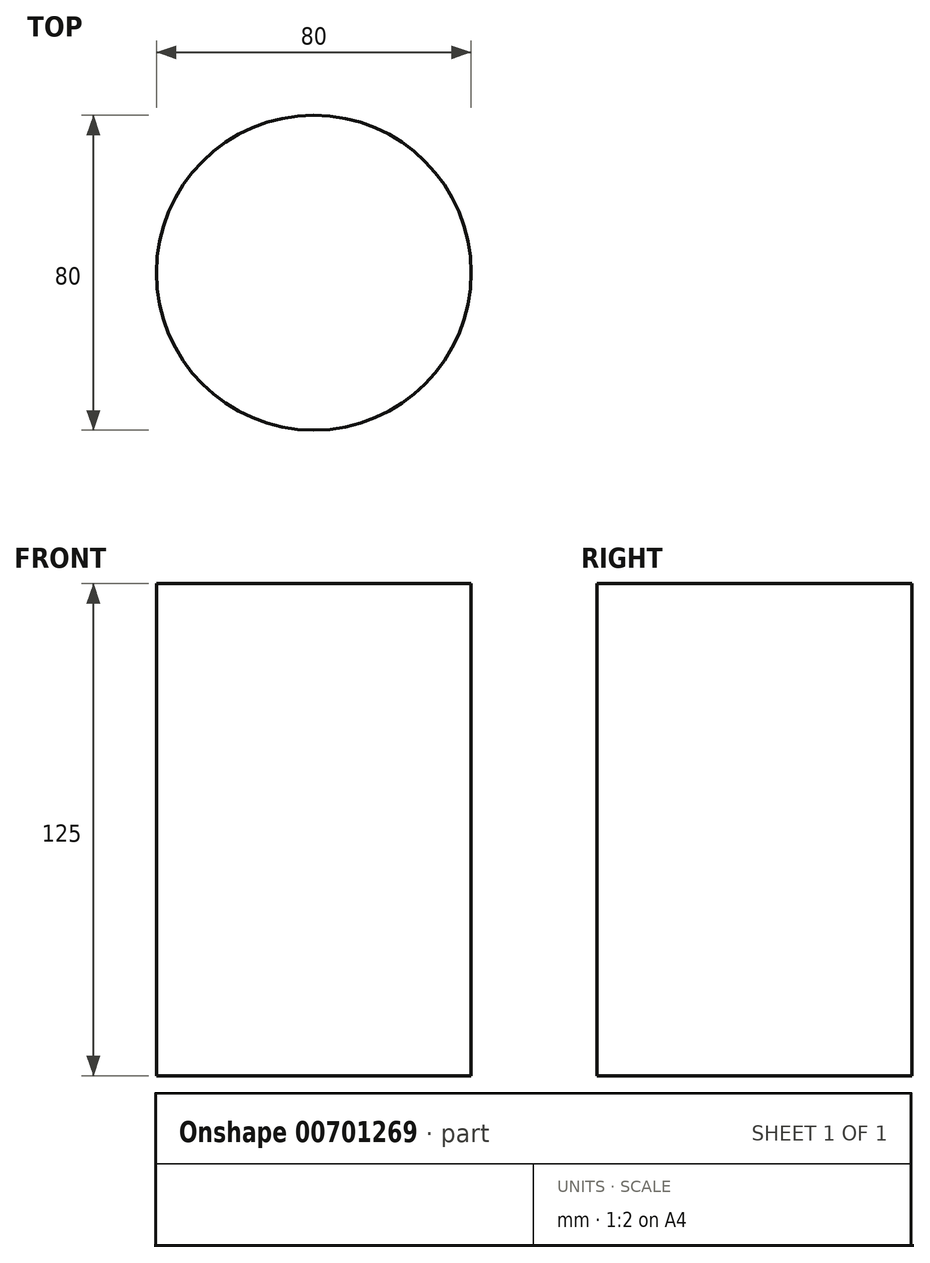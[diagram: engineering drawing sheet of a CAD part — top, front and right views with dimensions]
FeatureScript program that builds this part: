
annotation { "Feature Type Name" : "Feature", "Feature Type Description" : "" }
export const myFeature = defineFeature(function(context is Context, id is Id, definition is map)
    precondition{}
    {
        {
            var Q0;
            Q0=qCreatedBy(makeId("Top.planeOp"),FACE);
            var sketch = newSketch(context, id + "F0", { "sketchPlane" : qUnion([Q0])});
            skCircle(sketch, "E0", {"center": v(0, 0) * mm, "radius": 40 * mm});
            skSolve(sketch);
        }
        {
            var Q0;
            Q0 = qSketchRegion(id + "F0", true);
            extrude(context, id + "F1", {"entities" : qUnion([Q0]), "depth" : 125 * mm, "offsetDistance" : 25 * mm});
        }
    });
